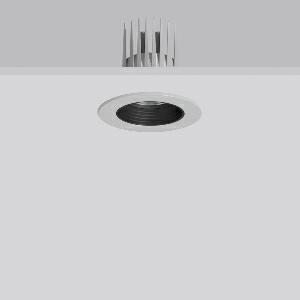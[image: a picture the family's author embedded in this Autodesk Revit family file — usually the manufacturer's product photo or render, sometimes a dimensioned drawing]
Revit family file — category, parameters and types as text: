
# Revit family: heledon_mini_e_901743_004_3_76_1d28
name_source: partatom
category: Lighting Fixtures
units: mm (PartAtom-declared; Revit-internal decimal feet)

## family parameters
Cut with Voids When Loaded = No
Host = Face
Light Source = No
Part Type = Normal
Room Calculation Point = No
Round Connector Dimension = Use Diameter
Shared = No

## types (1)
- HELEDON mini E (1 x LED Modul 935, 2250 lm, 3500)
    Apparent Load = 20 VA
    Approval mark = CE
    CIE Flux Codes = 99 100 100 100 100
    Color Rendering = 92
    Color Temperature = 3500
    Default Elevation = 1800 mm
    Description = Series: HELEDON mini
Round recessed downlight. Housing: die-cast aluminium, powder-coated. Black plastic ring and recessed LED to prevent glare from the side. Optical assembly with lens made of plastic (polycarbonate) for the best homogeneous light distribution - can be changed without tools. Best colour rendering index Ra>90. Suitable for Recessed ceiling mounting. Installation without tools thanks to spring fastening system. Including separate LED converter with connecting cable 600 mm.High quality converter without flickering and stroboscopic effect. Through-wiring box (5 pole) available as accessory. The following accessories can be mounted without use of tools: interchangeable lenses, decorative glasses, honeycomb louvre, clear and frosted diffusers, white interchangeable plastic ring. 
Colour: silver
Diameter: 124 mm
Height: 3 mm
Cut-out diameter: 114 mm
Recess height: 170 mm
Luminaire: recess height: 120 mm
Lamp: LED
Socket: without socket
Colour temperature: 3500K
Colour rendering index (CRI): 92
System power: 20 W
Rated luminous flux: 2250 lm
Luminous efficiency: 113 lm/W
Control gear: Converter, dimmable, DALI
Protection class: II
Type of protection: IP 20
    Height = 0 mm  [stored 0 ft]
    Lamp = 1 x LED Modul 935
    Lamp Light Flux = 2250 lm
    Lamp count = 1
    Length = 124 mm  [stored 0.406824 ft]
    Lifetime = 50000 h
    Luminous efficacy = 113 lm/W
    Manufacturer = RZB
    ModVariant = No
    Model = 901743.004.3.76
    Mounting Place = Ceiling
    Mounting Type = Recessed
    Number of Poles = 1
    OnlyDefault = Yes
    Power Factor = 1
    Product Name = HELEDON mini E
    Product group = Recessed downlights
    ProductGroupID = 402
    Protection Class = Protection class II
    Protection Degree = IP 20
    RLX_Detail_Level = 1
    RLX_Emergency_Light_Flux = 0 lm
    RLX_Emergency_Type = 0
    RLX_Emergency_Type_DB = No
    RlxData = <blob elided: 124361 chars, md5=ae4ed97e>
    Socket = socket
    Standby Power = 0 W
    System Light Flux = 2250 lm
    System Power = 20 W
    Type Comments = Product without accessories
    Type Image = 901656.004.jpg
    URL = http://relux.com
    VarID = ---
    Voltage = 230 V
    Voltage Range = 220-240 V
    Weight = 0.00 kg
    Width = 0 mm  [stored 0 ft]

note: [stored X ft] marks values corroborated as IEEE doubles in the binary element streams (Revit-internal decimal feet)

## geometry (parser evidence)
native form markers: Blend x4, Sweep x12
no freeform markers — native parametric forms only
